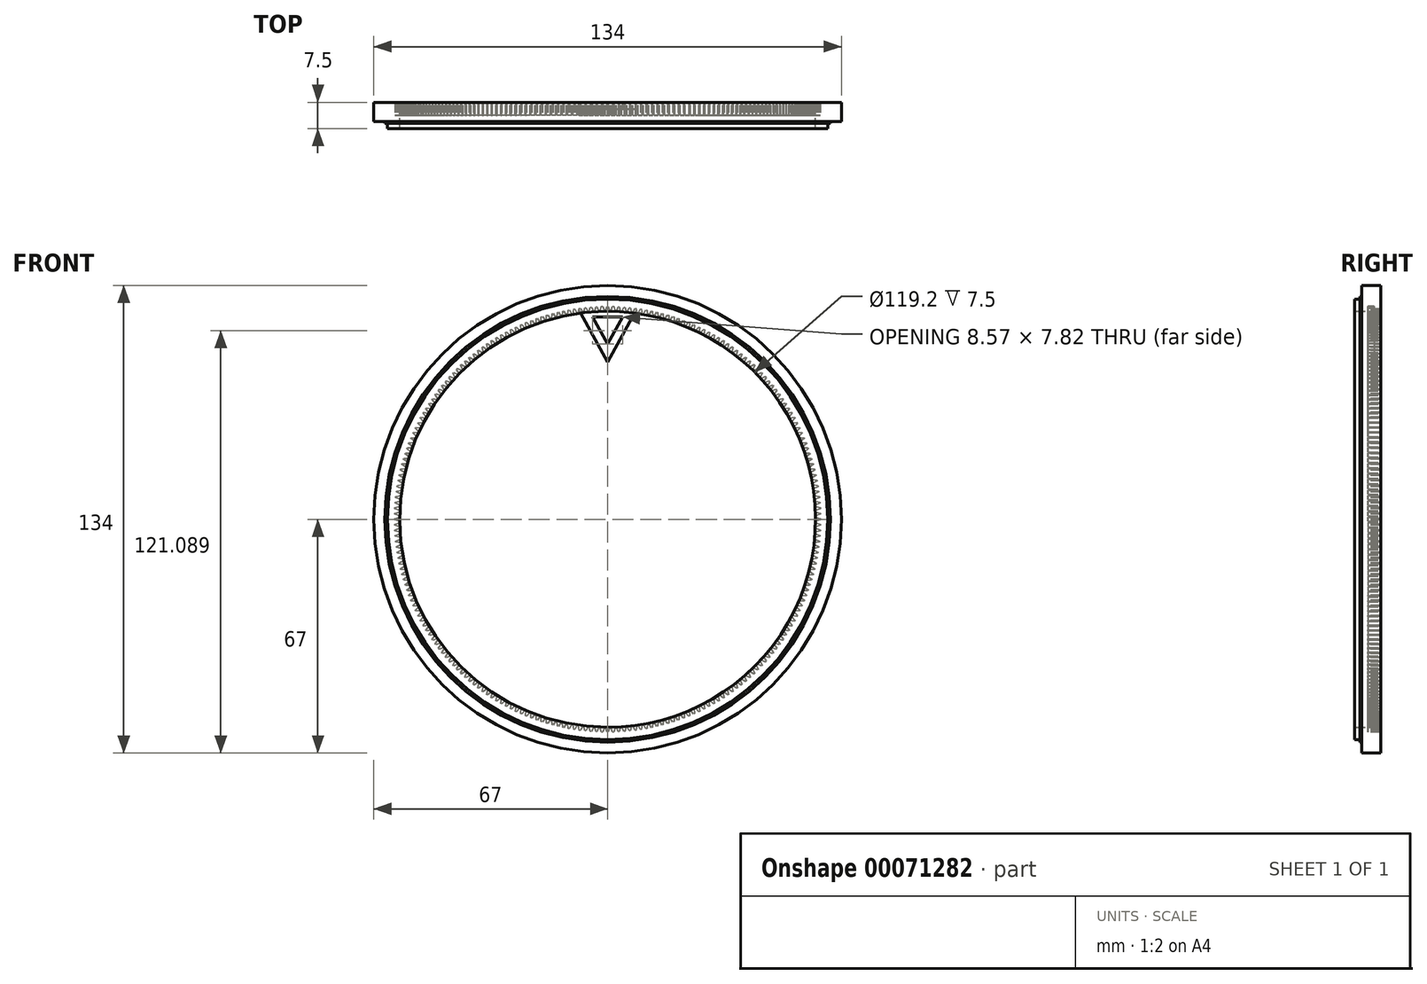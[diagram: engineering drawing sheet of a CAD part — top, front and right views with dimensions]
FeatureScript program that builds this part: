
annotation { "Feature Type Name" : "Feature", "Feature Type Description" : "" }
export const myFeature = defineFeature(function(context is Context, id is Id, definition is map)
    precondition{}
    {
        {
            var Q0;
            Q0=qCreatedBy(makeId("Front.planeOp"),FACE);
            var sketch = newSketch(context, id + "F0", { "sketchPlane" : qUnion([Q0])});
            skCircle(sketch, "E0", {"center": v(0, 0) * mm, "radius": 59.6 * mm});
            skCircle(sketch, "E1", {"center": v(0, 0) * mm, "radius": 67 * mm});
            skSolve(sketch);
        }
        {
            var Q0;
            Q0=makeQuery(id+"F0.imprint","IMPRINT",FACE,{"disambiguationData":[TD([[makeQuery(id+"F0.imprint","IMPRINT",EDGE,{"derivedFrom":sQuery(id+"F0.wireOp",EDGE,"E0")}),-1.0]])]});
            extrude(context, id + "F1", {"entities" : qUnion([Q0]), "endBound" : BoundingType.SYMMETRIC, "depth" : 7.5 * mm});
        }
        {
            var Q0;
            Q0=makeQuery(id+"F1.opExtrude","CAP_FACE",FACE,{"disambiguationData":[OSD([sQuery(id+"F0.wireOp",EDGE,"E0"),sQuery(id+"F0.wireOp",EDGE,"E1")])],"isStart":false});
            var sketch = newSketch(context, id + "F2", { "sketchPlane" : qUnion([Q0])});
            skCircle(sketch, "E2", {"center": v(0, 0) * mm, "radius": 63.12 * mm});
            skCircle(sketch, "E3", {"center": v(0, 0) * mm, "radius": 63.88 * mm});
            skSolve(sketch);
        }
        {
            var Q0;
            Q0=makeQuery(id+"F2.imprint","IMPRINT",FACE,{"disambiguationData":[TD([[makeQuery(id+"F2.imprint","IMPRINT",EDGE,{"derivedFrom":sQuery(id+"F2.wireOp",EDGE,"E2")}),-1.0]])]});
            extrude(context, id + "F3", {"entities" : qUnion([Q0]), "operationType" : NewBodyOperationType.REMOVE, "oppositeDirection" : true, "depth" : 1.5 * mm});
        }
        {
            var Q0;
            {var subQ0=sQuery(id+"F0.wireOp",EDGE,"E1");Q0=makeQuery(id+"F3.boolean.opBoolean","SPLIT",FACE,{"disambiguationData":[TD([makeQuery(id+"F1.opExtrude","SWEPT_FACE",FACE,{"disambiguationData":[OSD([subQ0])]})])],"derivedFrom":makeQuery(id+"F1.opExtrude","CAP_FACE",FACE,{"disambiguationData":[OSD([sQuery(id+"F0.wireOp",EDGE,"E0"),subQ0])],"isStart":false})});}
            extrude(context, id + "F4", {"entities" : qUnion([Q0]), "operationType" : NewBodyOperationType.REMOVE, "oppositeDirection" : true, "depth" : 2 * mm});
        }
        {
            var Q0;
            Q0=qCreatedBy(makeId("Front.planeOp"),FACE);
            var sketch = newSketch(context, id + "F5", { "sketchPlane" : qUnion([Q0])});
            skCircle(sketch, "E4", {"center": v(0, 0) * mm, "radius": 61 * mm, "construction": true});
            skLineSegment(sketch, "E5", {"start": v(0, 0) * mm, "end": v(61, 0) * mm, "construction": true});
            skLineSegment(sketch, "E6", {"start": v(61, 0.15) * mm, "end": v(61, -0.15) * mm});
            skPoint(sketch, "E7", {"position": v(59.4, 0) * mm});
            skLineSegment(sketch, "E8", {"start": v(59.4, 0.68) * mm, "end": v(59.4, -0.67) * mm});
            skLineSegment(sketch, "E9", {"start": v(59.4, 0.68) * mm, "end": v(61, 0.15) * mm});
            skLineSegment(sketch, "E10", {"start": v(61, -0.15) * mm, "end": v(59.4, -0.67) * mm});
            skSolve(sketch);
        }
        {
            var Q0;
            Q0=makeQuery(id+"F5.imprint","IMPRINT",FACE,{"disambiguationData":[TD([[makeQuery(id+"F5.imprint","IMPRINT",EDGE,{"derivedFrom":sQuery(id+"F5.wireOp",EDGE,"E6")}),-1.0]])]});
            extrude(context, id + "F6", {"entities" : qUnion([Q0]), "operationType" : NewBodyOperationType.REMOVE, "oppositeDirection" : true, "depth" : 6.5 * mm});
        }
        {
            var Q0;
            Q0=makeQuery(id+"F6.boolean.opBoolean","COPY",FACE,{"derivedFrom":makeQuery(id+"F6.opExtrude","SWEPT_FACE",FACE,{"disambiguationData":[OSD([sQuery(id+"F5.wireOp",EDGE,"E9")])]})});
            var Q1;
            Q1=makeQuery(id+"F6.boolean.opBoolean","COPY",FACE,{"derivedFrom":makeQuery(id+"F6.opExtrude","SWEPT_FACE",FACE,{"disambiguationData":[OSD([sQuery(id+"F5.wireOp",EDGE,"E6")])]})});
            var Q2;
            Q2=makeQuery(id+"F6.boolean.opBoolean","COPY",FACE,{"derivedFrom":makeQuery(id+"F6.opExtrude","SWEPT_FACE",FACE,{"disambiguationData":[OSD([sQuery(id+"F5.wireOp",EDGE,"E10")])]})});
            var Q3;
            Q3=makeQuery(id+"F6.boolean.opBoolean","COPY",FACE,{"derivedFrom":makeQuery(id+"F6.opExtrude","CAP_FACE",FACE,{"disambiguationData":[OSD([sQuery(id+"F5.wireOp",EDGE,"E6"),sQuery(id+"F5.wireOp",EDGE,"E8"),sQuery(id+"F5.wireOp",EDGE,"E9"),sQuery(id+"F5.wireOp",EDGE,"E10")])],"isStart":true})});
            var Q4;
            Q4=makeQuery(id+"F1.opExtrude","CAP_EDGE",EDGE,{"disambiguationData":[OSD([sQuery(id+"F0.wireOp",EDGE,"E0")])],"isStart":false});
            circularPattern(context, id + "F7", {"faces" : qUnion([Q0, Q1, Q2, Q3]), "axis" : qUnion([Q4]), "angle" : 360 * degree, "instanceCount" : 240, "equalSpace" : true, "patternType" : PatternType.FACE});
        }
        {
            var Q0;
            Q0=makeQuery(id+"F1.opExtrude","CAP_FACE",FACE,{"disambiguationData":[OSD([sQuery(id+"F0.wireOp",EDGE,"E0"),sQuery(id+"F0.wireOp",EDGE,"E1")])],"isStart":true});
            var sketch = newSketch(context, id + "F8", { "sketchPlane" : qUnion([Q0])});
            skCircle(sketch, "E11.0", {"center": v(0, 0) * mm, "radius": 61 * mm, "construction": true});
            skLineSegment(sketch, "E12", {"start": v(0, 45) * mm, "end": v(0, 0) * mm, "construction": true});
            skLineSegment(sketch, "E13", {"start": v(0, 0) * mm, "end": v(8.49, 60.4) * mm, "construction": true});
            skLineSegment(sketch, "E14", {"start": v(8.49, 60.4) * mm, "end": v(0, 45) * mm});
            skLineSegment(sketch, "E15.MirrorCS", {"start": v(-8.49, 60.4) * mm, "end": v(0, 45) * mm});
            skLineSegment(sketch, "E16.0", {"start": v(4.28, 57.95) * mm, "end": v(0.12, 58) * mm});
            skLineSegment(sketch, "E16.1", {"start": v(4.28, 57.95) * mm, "end": v(0, 50.18) * mm});
            skLineSegment(sketch, "E16.2", {"start": v(-4.28, 57.95) * mm, "end": v(0, 50.18) * mm});
            skLineSegment(sketch, "E16.3", {"start": v(-4.28, 57.95) * mm, "end": v(-0.12, 58) * mm});
            skLineSegment(sketch, "E17", {"start": v(0.12, 58) * mm, "end": v(-0.12, 58) * mm});
            skLineSegment(sketch, "E18", {"start": v(-8.49, 60.4) * mm, "end": v(0, 62.97) * mm});
            skLineSegment(sketch, "E19", {"start": v(0, 62.97) * mm, "end": v(8.49, 60.4) * mm});
            skSolve(sketch);
        }
        {
            var Q0;
            Q0=makeQuery(id+"F8.imprint","IMPRINT",FACE,{"disambiguationData":[TD([[makeQuery(id+"F8.imprint","IMPRINT",EDGE,{"derivedFrom":sQuery(id+"F8.wireOp",EDGE,"E16.0")}),-1.0]])]});
            extrude(context, id + "F9", {"entities" : qUnion([Q0]), "operationType" : NewBodyOperationType.ADD, "oppositeDirection" : true, "depth" : 2 * mm});
        }
    });
